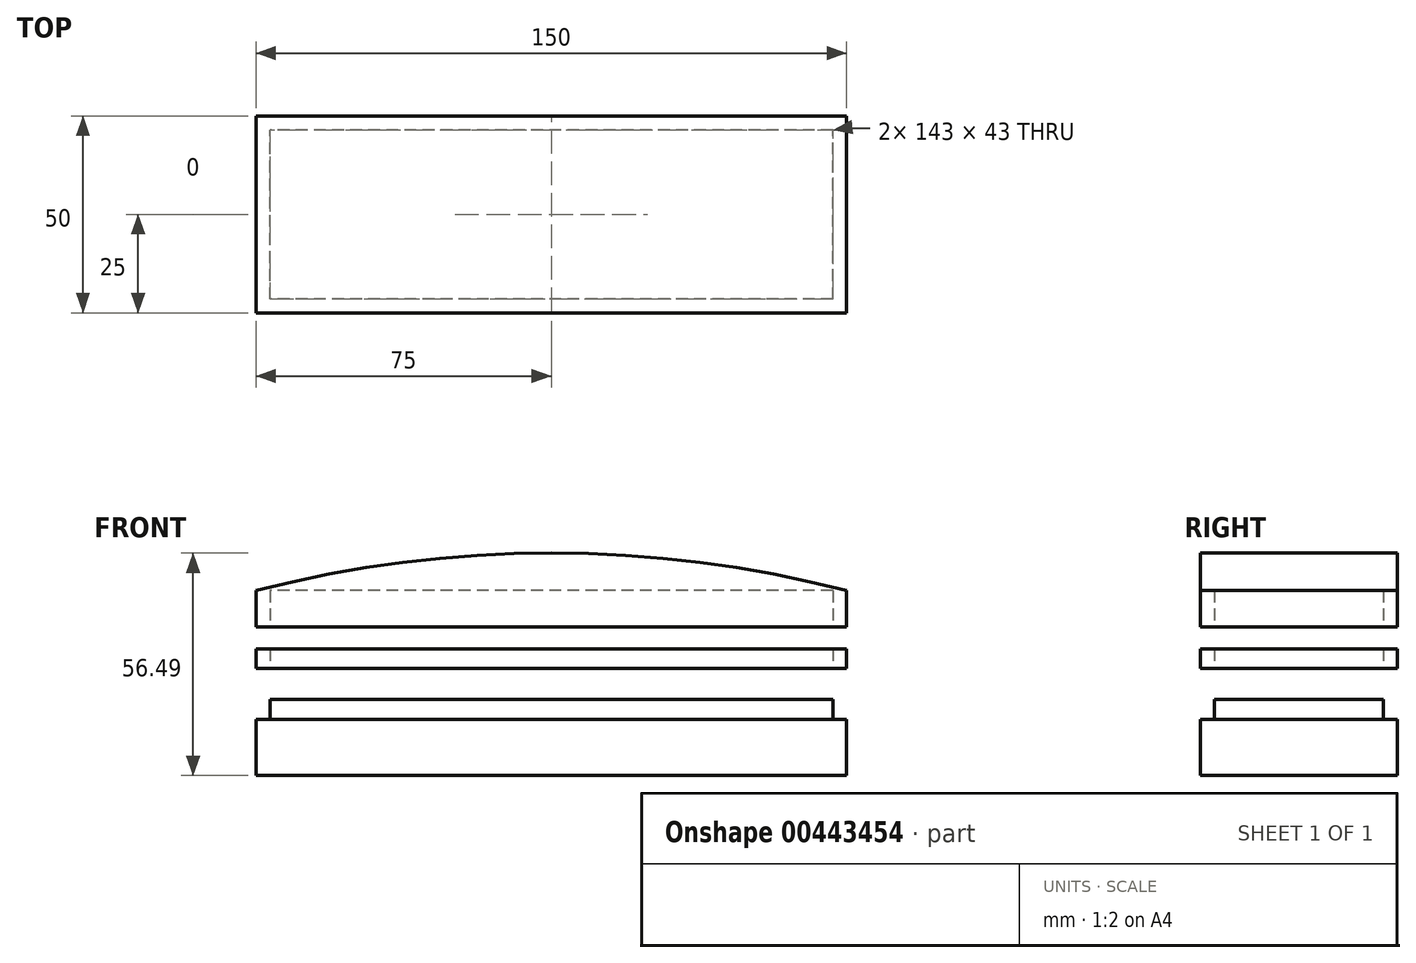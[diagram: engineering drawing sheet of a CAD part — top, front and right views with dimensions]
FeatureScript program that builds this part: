
annotation { "Feature Type Name" : "Feature", "Feature Type Description" : "" }
export const myFeature = defineFeature(function(context is Context, id is Id, definition is map)
    precondition{}
    {
        {
            var Q0;
            Q0=qCreatedBy(makeId("Front.planeOp"),FACE);
            var sketch = newSketch(context, id + "F0", { "sketchPlane" : qUnion([Q0])});
            skLineSegment(sketch, "E0.bottom", {"start": v(75, 7.13) * mm, "end": v(-75, 7.13) * mm});
            skLineSegment(sketch, "E0.top", {"start": v(75, -7.14) * mm, "end": v(-75, -7.14) * mm});
            skLineSegment(sketch, "E0.left", {"start": v(75, 7.13) * mm, "end": v(75, -7.13) * mm});
            skLineSegment(sketch, "E0.right", {"start": v(-75, 7.13) * mm, "end": v(-75, -7.14) * mm});
            skPoint(sketch, "E0.middle", {"position": v(0, 0) * mm});
            skSolve(sketch);
        }
        {
            var Q0;
            Q0=qSketchRegion(id+"F0",true);
            extrude(context, id + "F1", {"entities" : qUnion([Q0]), "depth" : 25 * mm});
        }
        {
            var Q0;
            Q0=makeQuery(id+"F1.opExtrude","CAP_FACE",FACE,{"disambiguationData":[OSD([sQuery(id+"F0.wireOp",EDGE,"E0.bottom"),sQuery(id+"F0.wireOp",EDGE,"E0.top"),sQuery(id+"F0.wireOp",EDGE,"E0.left"),sQuery(id+"F0.wireOp",EDGE,"E0.right")])],"isStart":true});
            extrude(context, id + "F2", {"entities" : qUnion([Q0]), "operationType" : NewBodyOperationType.ADD, "depth" : 25 * mm});
        }
        {
            var Q0;
            {var subQ0=sQuery(id+"F0.wireOp",EDGE,"E0.top");Q0=makeQuery(id+"F2.boolean.opBoolean","MERGE",FACE,{"derivedFrom":[makeQuery(id+"F1.opExtrude","SWEPT_FACE",FACE,{"disambiguationData":[OSD([subQ0])]}),makeQuery(id+"F2.opExtrude","SWEPT_FACE",FACE,{"disambiguationData":[OSD([subQ0])]})]});}
            var sketch = newSketch(context, id + "F3", { "sketchPlane" : qUnion([Q0])});
            skLineSegment(sketch, "E1.bottom", {"start": v(-71.5, -21.5) * mm, "end": v(71.5, -21.5) * mm});
            skLineSegment(sketch, "E1.top", {"start": v(-71.5, 21.5) * mm, "end": v(71.5, 21.5) * mm});
            skLineSegment(sketch, "E1.left", {"start": v(-71.5, -21.5) * mm, "end": v(-71.5, 21.5) * mm});
            skLineSegment(sketch, "E1.right", {"start": v(71.5, -21.5) * mm, "end": v(71.5, 21.5) * mm});
            skPoint(sketch, "E1.middle", {"position": v(0, 0) * mm});
            skSolve(sketch);
        }
        {
            var Q0;
            Q0=qSketchRegion(id+"F3",true);
            extrude(context, id + "F4", {"entities" : qUnion([Q0]), "operationType" : NewBodyOperationType.ADD, "oppositeDirection" : true, "depth" : 19.27 * mm});
        }
        {
            var Q0;
            Q0=qCreatedBy(makeId("Top.planeOp"),FACE);
            cPlane(context, id + "F5", {"entities" : qUnion([Q0]), "cplaneType" : CPlaneType.OFFSET, "offset" : 20 * mm, "width" : 150 * mm, "height" : 150 * mm});
        }
        {
            var Q0;
            Q0=qCreatedBy(id+"F5.planeOp",FACE);
            var sketch = newSketch(context, id + "F6", { "sketchPlane" : qUnion([Q0])});
            skLineSegment(sketch, "E2.bottom", {"start": v(75, 25) * mm, "end": v(-75, 25) * mm});
            skLineSegment(sketch, "E2.top", {"start": v(75, -25) * mm, "end": v(-75, -25) * mm});
            skLineSegment(sketch, "E2.left", {"start": v(75, 25) * mm, "end": v(75, -25) * mm});
            skLineSegment(sketch, "E2.right", {"start": v(-75, 25) * mm, "end": v(-75, -25) * mm});
            skPoint(sketch, "E2.middle", {"position": v(0, 0) * mm});
            skLineSegment(sketch, "E3.bottom", {"start": v(71.5, 21.5) * mm, "end": v(-71.5, 21.5) * mm});
            skLineSegment(sketch, "E3.top", {"start": v(71.5, -21.5) * mm, "end": v(-71.5, -21.5) * mm});
            skLineSegment(sketch, "E3.left", {"start": v(71.5, 21.5) * mm, "end": v(71.5, -21.5) * mm});
            skLineSegment(sketch, "E3.right", {"start": v(-71.5, 21.5) * mm, "end": v(-71.5, -21.5) * mm});
            skSolve(sketch);
        }
        {
            var Q0;
            Q0=makeQuery(id+"F6.imprint","IMPRINT",FACE,{"disambiguationData":[TD([[makeQuery(id+"F6.imprint","IMPRINT",EDGE,{"derivedFrom":sQuery(id+"F6.wireOp",EDGE,"E2.bottom")}),1.0]])]});
            extrude(context, id + "F7", {"entities" : qUnion([Q0]), "depth" : 5 * mm});
        }
        {
            var Q0;
            Q0=qCreatedBy(makeId("Front.planeOp"),FACE);
            var sketch = newSketch(context, id + "F8", { "sketchPlane" : qUnion([Q0])});
            skLineSegment(sketch, "E4.bottom", {"start": v(75, 39.83) * mm, "end": v(-75, 39.83) * mm});
            skLineSegment(sketch, "E4.top", {"start": v(75, 30.56) * mm, "end": v(-75, 30.56) * mm});
            skLineSegment(sketch, "E4.left", {"start": v(75, 39.83) * mm, "end": v(75, 30.56) * mm});
            skLineSegment(sketch, "E4.right", {"start": v(-75, 39.83) * mm, "end": v(-75, 30.56) * mm});
            skPoint(sketch, "E4.middle", {"position": v(0, 35.2) * mm});
            skArc(sketch, "E5", {"start": v(75, 39.83) * mm, "mid": v(0, 49.36) * mm, "end": v(-75, 39.83) * mm});
            skSolve(sketch);
        }
        {
            var Q0;
            Q0=makeQuery(id+"F8.imprint","IMPRINT",FACE,{"disambiguationData":[TD([[makeQuery(id+"F8.imprint","IMPRINT",EDGE,{"derivedFrom":sQuery(id+"F8.wireOp",EDGE,"E4.bottom")}),-1.0]])]});
            var Q1;
            Q1=makeQuery(id+"F8.imprint","IMPRINT",FACE,{"disambiguationData":[TD([[makeQuery(id+"F8.imprint","IMPRINT",EDGE,{"derivedFrom":sQuery(id+"F8.wireOp",EDGE,"E4.bottom")}),1.0]])]});
            extrude(context, id + "F9", {"entities" : qUnion([Q0, Q1]), "depth" : 25 * mm});
        }
        {
            var Q0;
            Q0=makeQuery(id+"F9.opExtrude","CAP_FACE",FACE,{"disambiguationData":[OSD([sQuery(id+"F8.wireOp",EDGE,"E4.top"),sQuery(id+"F8.wireOp",EDGE,"E4.left"),sQuery(id+"F8.wireOp",EDGE,"E4.right"),sQuery(id+"F8.wireOp",EDGE,"E5")])],"isStart":true});
            extrude(context, id + "F10", {"entities" : qUnion([Q0]), "operationType" : NewBodyOperationType.ADD, "depth" : 25 * mm});
        }
        {
            var Q0;
            {var subQ0=sQuery(id+"F8.wireOp",EDGE,"E4.top");Q0=makeQuery(id+"F10.boolean.opBoolean","MERGE",FACE,{"derivedFrom":[makeQuery(id+"F9.opExtrude","SWEPT_FACE",FACE,{"disambiguationData":[OSD([subQ0])]}),makeQuery(id+"F10.opExtrude","SWEPT_FACE",FACE,{"disambiguationData":[OSD([subQ0])]})]});}
            var sketch = newSketch(context, id + "F11", { "sketchPlane" : qUnion([Q0])});
            skLineSegment(sketch, "E6.bottom", {"start": v(71.5, 21.5) * mm, "end": v(-71.5, 21.5) * mm});
            skLineSegment(sketch, "E6.top", {"start": v(71.5, -21.5) * mm, "end": v(-71.5, -21.5) * mm});
            skLineSegment(sketch, "E6.left", {"start": v(71.5, 21.5) * mm, "end": v(71.5, -21.5) * mm});
            skLineSegment(sketch, "E6.right", {"start": v(-71.5, 21.5) * mm, "end": v(-71.5, -21.5) * mm});
            skPoint(sketch, "E6.middle", {"position": v(0, 0) * mm});
            skSolve(sketch);
        }
        {
            var Q0;
            Q0=makeQuery(id+"F11.imprint","IMPRINT",FACE,{"disambiguationData":[TD([[makeQuery(id+"F11.imprint","IMPRINT",EDGE,{"derivedFrom":sQuery(id+"F11.wireOp",EDGE,"E6.bottom")}),1.0]])]});
            extrude(context, id + "F12", {"entities" : qUnion([Q0]), "operationType" : NewBodyOperationType.REMOVE, "oppositeDirection" : true, "depth" : 9.27 * mm});
        }
    });
